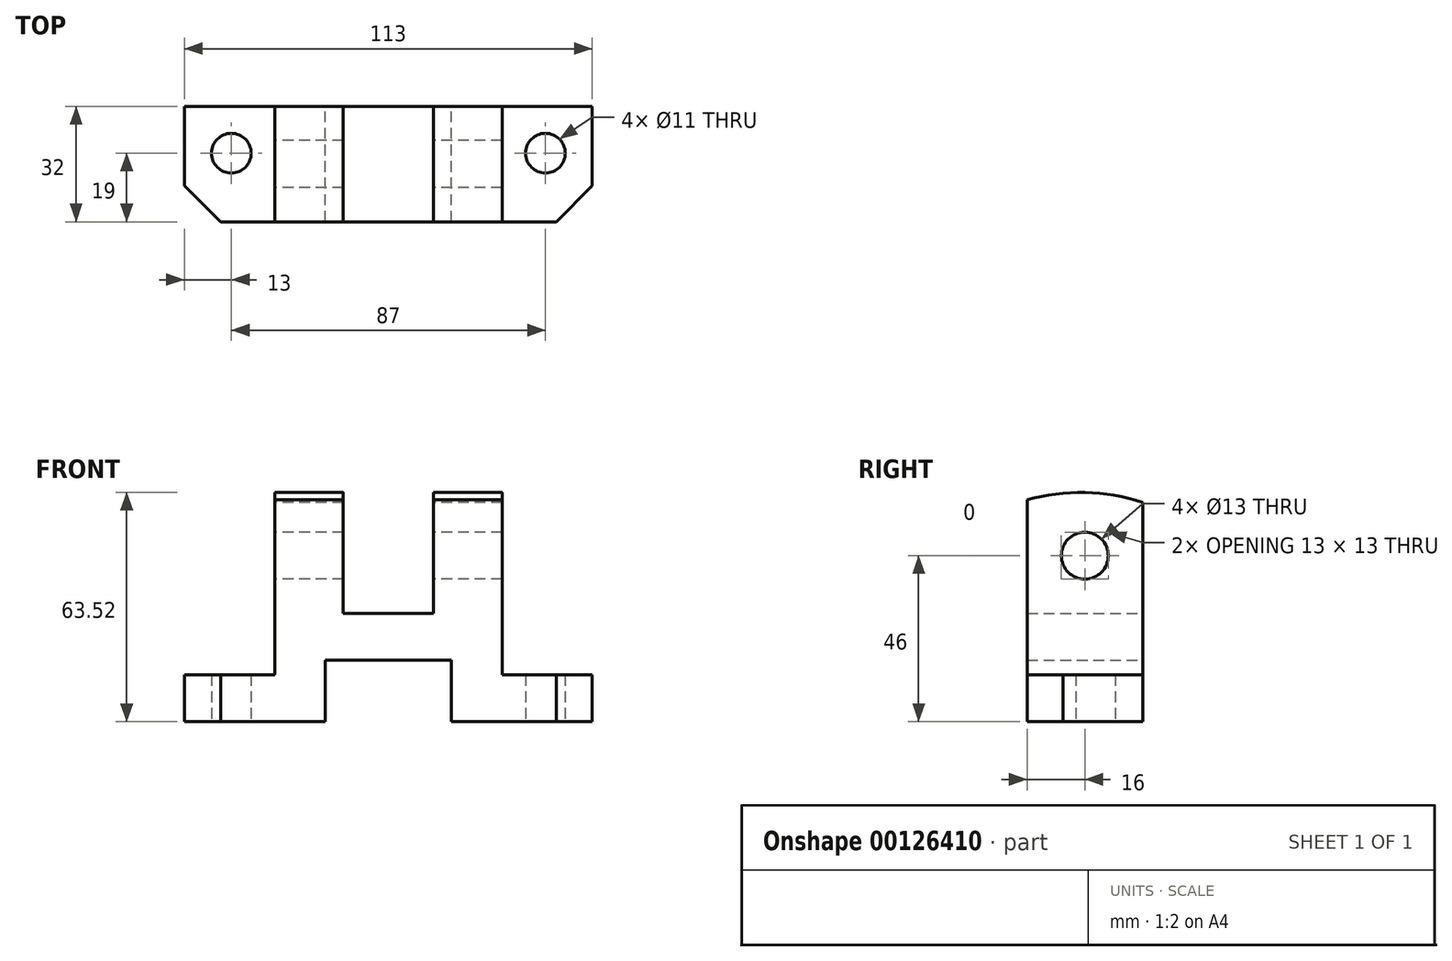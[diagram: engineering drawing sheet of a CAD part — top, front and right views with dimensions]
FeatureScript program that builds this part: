
annotation { "Feature Type Name" : "Feature", "Feature Type Description" : "" }
export const myFeature = defineFeature(function(context is Context, id is Id, definition is map)
    precondition{}
    {
        {
            var Q0;
            Q0=qCreatedBy(makeId("Front.planeOp"),FACE);
            var sketch = newSketch(context, id + "F0", { "sketchPlane" : qUnion([Q0])});
            skLineSegment(sketch, "E0", {"start": v(0, 0) * mm, "end": v(0, 13) * mm});
            skLineSegment(sketch, "E1", {"start": v(0, 13) * mm, "end": v(25, 13) * mm});
            skLineSegment(sketch, "E2", {"start": v(25, 13) * mm, "end": v(25, 64) * mm});
            skLineSegment(sketch, "E3", {"start": v(25, 64) * mm, "end": v(44, 64) * mm});
            skLineSegment(sketch, "E4", {"start": v(44, 64) * mm, "end": v(44, 30) * mm});
            skLineSegment(sketch, "E5", {"start": v(44, 30) * mm, "end": v(69, 30) * mm});
            skLineSegment(sketch, "E6", {"start": v(69, 30) * mm, "end": v(69, 64) * mm});
            skLineSegment(sketch, "E7", {"start": v(69, 64) * mm, "end": v(88, 64) * mm});
            skLineSegment(sketch, "E8", {"start": v(88, 64) * mm, "end": v(88, 13) * mm});
            skLineSegment(sketch, "E9", {"start": v(88, 13) * mm, "end": v(113, 13) * mm});
            skLineSegment(sketch, "E10", {"start": v(113, 13) * mm, "end": v(113, 0) * mm});
            skLineSegment(sketch, "E11", {"start": v(113, 0) * mm, "end": v(74, 0) * mm});
            skLineSegment(sketch, "E12", {"start": v(74, 0) * mm, "end": v(74, 17) * mm});
            skLineSegment(sketch, "E13", {"start": v(74, 17) * mm, "end": v(39, 17) * mm});
            skLineSegment(sketch, "E14", {"start": v(39, 17) * mm, "end": v(39, 0) * mm});
            skLineSegment(sketch, "E15", {"start": v(39, 0) * mm, "end": v(0, 0) * mm});
            skSolve(sketch);
        }
        {
            var Q0;
            Q0 = qSketchRegion(id + "F0", true);
            extrude(context, id + "F1", {"entities" : qUnion([Q0]), "depth" : 32 * mm});
        }
        {
            var Q0;
            Q0=qCreatedBy(makeId("Top.planeOp"),FACE);
            var sketch = newSketch(context, id + "F2", { "sketchPlane" : qUnion([Q0])});
            skCircle(sketch, "E16", {"center": v(13, -13) * mm, "radius": 5.5 * mm});
            skCircle(sketch, "E17", {"center": v(100, -13) * mm, "radius": 5.5 * mm});
            skLineSegment(sketch, "E18", {"start": v(0, -22) * mm, "end": v(10, -32) * mm});
            skLineSegment(sketch, "E19", {"start": v(103, -32) * mm, "end": v(113, -22) * mm});
            skLineSegment(sketch, "E20.0", {"start": v(0, 0) * mm, "end": v(25, 0) * mm});
            skLineSegment(sketch, "E21.0", {"start": v(0, -32) * mm, "end": v(25, -32) * mm});
            skLineSegment(sketch, "E22.0", {"start": v(0, -32) * mm, "end": v(0, 0) * mm});
            skLineSegment(sketch, "E23.0", {"start": v(88, -32) * mm, "end": v(113, -32) * mm});
            skLineSegment(sketch, "E24.0", {"start": v(113, -32) * mm, "end": v(113, 0) * mm});
            skLineSegment(sketch, "E25.0", {"start": v(88, 0) * mm, "end": v(113, 0) * mm});
            skSolve(sketch);
        }
        {
            var Q0;
            Q0 = qSketchRegion(id + "F2", true);
            extrude(context, id + "F3", {"entities" : qUnion([Q0]), "operationType" : NewBodyOperationType.REMOVE, "depth" : 25 * mm});
        }
        {
            var Q0;
            Q0=qCreatedBy(makeId("Right.planeOp"),FACE);
            var sketch = newSketch(context, id + "F4", { "sketchPlane" : qUnion([Q0])});
            skCircle(sketch, "E26", {"center": v(-16, 46) * mm, "radius": 6.5 * mm});
            skArc(sketch, "E27", {"start": v(0, 60.75) * mm, "mid": v(-15.95, 63.5) * mm, "end": v(-32, 61.44) * mm});
            skLineSegment(sketch, "E28.0", {"start": v(-32, 64) * mm, "end": v(-32, 13) * mm});
            skLineSegment(sketch, "E29.0", {"start": v(0, 64) * mm, "end": v(0, 13) * mm});
            skLineSegment(sketch, "E30.0", {"start": v(-32, 64) * mm, "end": v(0, 64) * mm});
            skSolve(sketch);
        }
        {
            var Q0;
            Q0 = qSketchRegion(id + "F4", true);
            extrude(context, id + "F5", {"entities" : qUnion([Q0]), "operationType" : NewBodyOperationType.REMOVE, "depth" : 132.4 * mm});
        }
    });
